# Revit family: Spray Bodies RD1800-S-P-45-F Series
name_source: partatom
category: Acessórios do tubo
units: mm (PartAtom-declared; Revit-internal decimal feet)

## family parameters
Com base no plano de trabalho = Não
Compartilhado = Não
Corte com vazios quando carregada = Não
Cota do conector redondo = Utilizar diâmetro
Número OmniClass = 23.60.30.11.14
Sempre na vertical = Sim
Tipo de parte = Normal
Título OmniClass = Pipework Fittings

## types (3) — shared parameters
AA1 = 135.00°
Black Plastic = Black Plastic
Black Plastic 2 = Black Plastic 2
Conection = 2
DD1 = 1
DD10 = 3
DD13 = 2
DD2 = 1
DD3 = 2
DD7 = 1
DT1 = 1
DT2 = 1
DT3 = 1
DT4 = 1
DT6 = 2
DT7 = 3
R-VAN = Sim
R1 = 1
R2 = 3
R3 = 2
R4 = 1
R5 = 1
RN = 1
RainBird: Product Link = https://store.rainbird.com
SupportProjetos: Level of Detail = LOD 300
SupportProjetos: Reviw = R01
SupportProjetos: Reviw Date = 15/11/2020
URL = https://www.rainbird.com
White Plastic = White Plastic
zero-valued in all types: DD5, DD6, DT5, DT8, Elevação padrão, RT

## per-type parameters (varying)
| type | 180 | 1804 | 1806 | 1812 | Body height | DD11 | DD9 | Descrição | H1 | Model | Modelo | Pop up height | RainBird: Description | Side inlet |
| RD1804-S-P-45-F | Sim | Sim | Não | Não | 15 | 0 | 1 | Spray Bodies Serie RD1800 - Model RD1804-S-P-45-F | 5 | 1804 | RD1804-S-P-45-F | 10 | Spray Bodies Serie RD1800 - Model RD1804-S-P-45-F | Não |
| RD1806-S-P45-F | Sim | Não | Sim | Não | 24 | 0 | 1 | Spray Bodies Serie RD1800 - Model RD1806-S-P-45-F | 8 | 1806 | RD1806-S-P-45-F | 15 | Spray Bodies Serie RD1800 - Model RD1806-S-P-45-F | Sim |
| RD1812-S-P-45-F | Não | Não | Não | Sim | 41 | 1 | 2 | Spray Bodies Serie ED1800 - Model RD1812-S-P-45-F | 14 | 1812 | RD1812-S-P-P45-F | 31 | Spray Bodies Serie ED1800 - Model RD1812-S-P-45-F | Sim |
